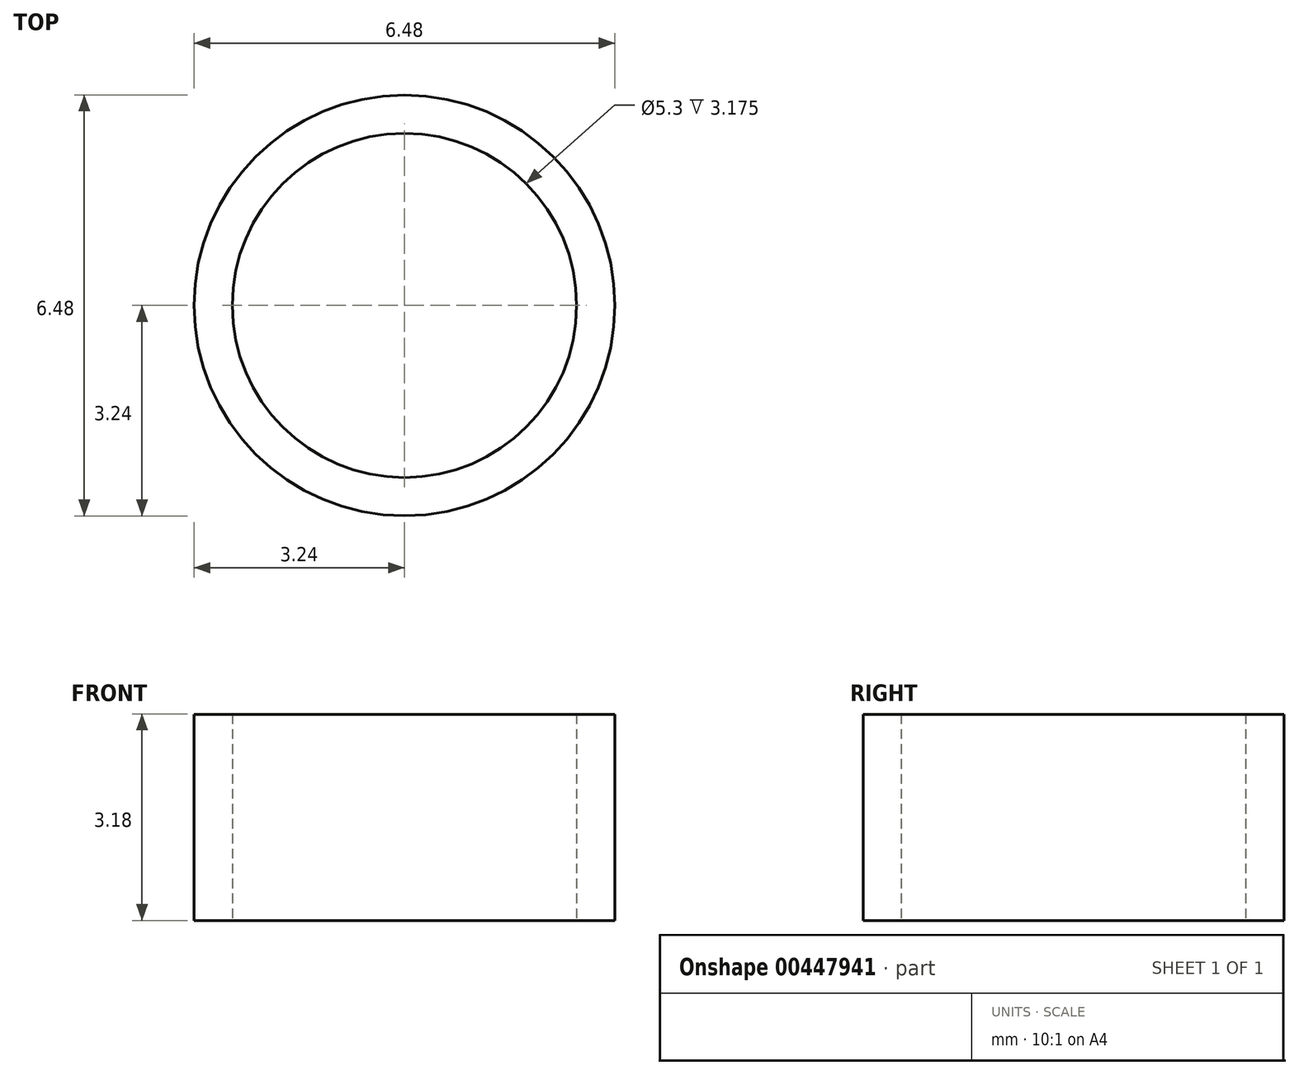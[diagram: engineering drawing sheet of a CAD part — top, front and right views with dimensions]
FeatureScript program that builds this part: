
annotation { "Feature Type Name" : "Feature", "Feature Type Description" : "" }
export const myFeature = defineFeature(function(context is Context, id is Id, definition is map)
    precondition{}
    {
        {
            var Q0;
            Q0=qCreatedBy(makeId("Top.planeOp"),FACE);
            var sketch = newSketch(context, id + "F0", { "sketchPlane" : qUnion([Q0])});
            skCircle(sketch, "E0", {"center": v(0, 0) * mm, "radius": 2.65 * mm});
            skCircle(sketch, "E1", {"center": v(0, 0) * mm, "radius": 3.24 * mm});
            skSolve(sketch);
        }
        {
            var Q0;
            Q0=makeQuery(id+"F0.imprint","IMPRINT",FACE,{"disambiguationData":[TD([[makeQuery(id+"F0.imprint","IMPRINT",EDGE,{"derivedFrom":sQuery(id+"F0.wireOp",EDGE,"E0")}),-1.0]])]});
            extrude(context, id + "F1", {"entities" : qUnion([Q0]), "depth" : 3.17 * mm, "offsetDistance" : 25.4 * mm});
        }
    });
